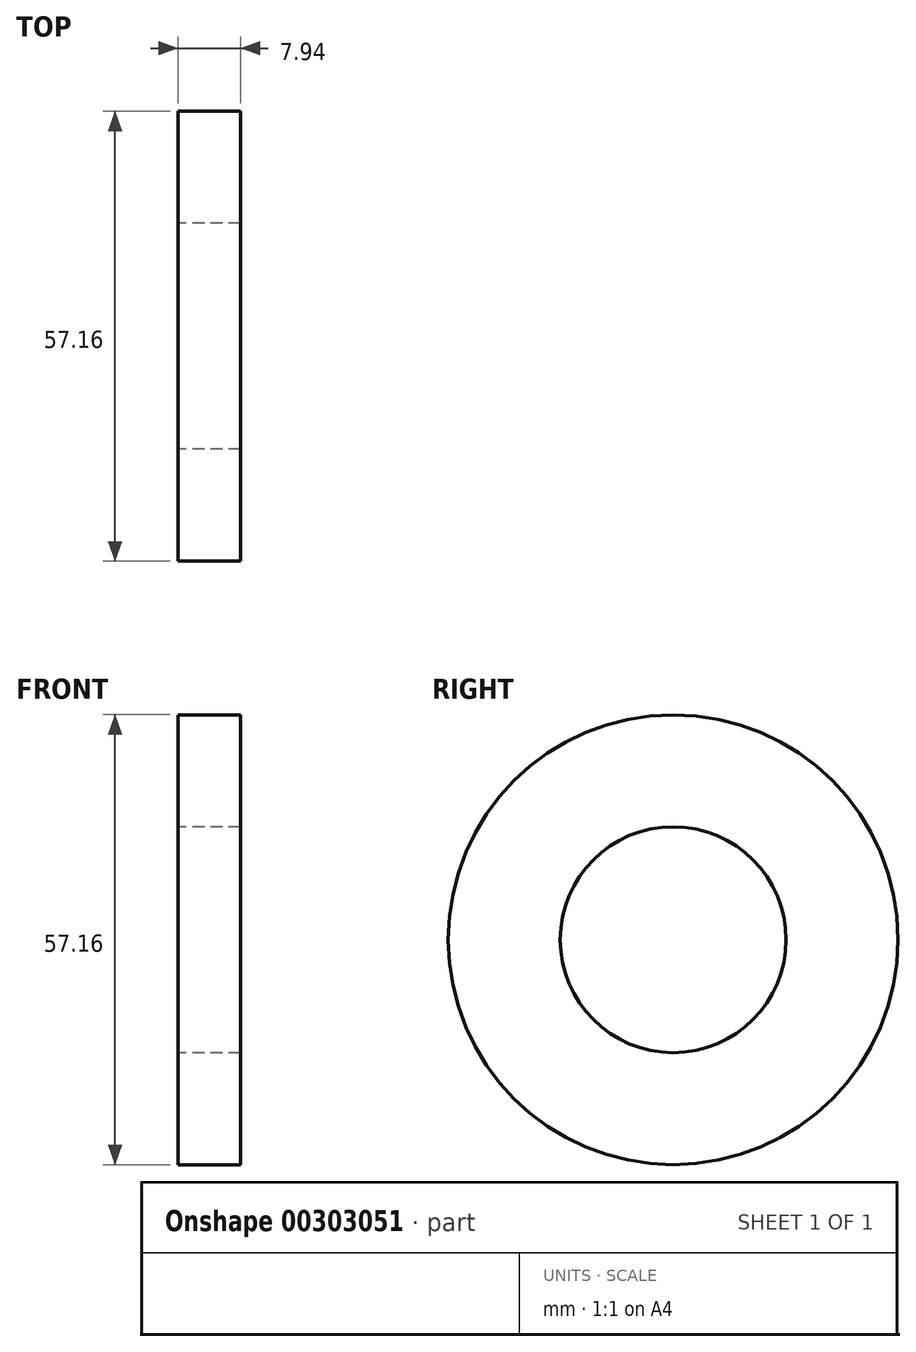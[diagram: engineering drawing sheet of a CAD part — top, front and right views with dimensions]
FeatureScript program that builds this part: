
annotation { "Feature Type Name" : "Feature", "Feature Type Description" : "" }
export const myFeature = defineFeature(function(context is Context, id is Id, definition is map)
    precondition{}
    {
        {
            var Q0;
            Q0=qCreatedBy(makeId("Right.planeOp"),FACE);
            var sketch = newSketch(context, id + "F0", { "sketchPlane" : qUnion([Q0])});
            skCircle(sketch, "E0", {"center": v(0, 0) * mm, "radius": 28.58 * mm});
            skCircle(sketch, "E1", {"center": v(0, 0) * mm, "radius": 14.35 * mm});
            skSolve(sketch);
        }
        {
            var Q0;
            Q0=makeQuery(id+"F0.imprint","IMPRINT",FACE,{"disambiguationData":[TD([[makeQuery(id+"F0.imprint","IMPRINT",EDGE,{"derivedFrom":sQuery(id+"F0.wireOp",EDGE,"E0")}),1.0]])]});
            extrude(context, id + "F1", {"entities" : qUnion([Q0]), "depth" : 7.94 * mm, "symmetric" : true});
        }
    });
